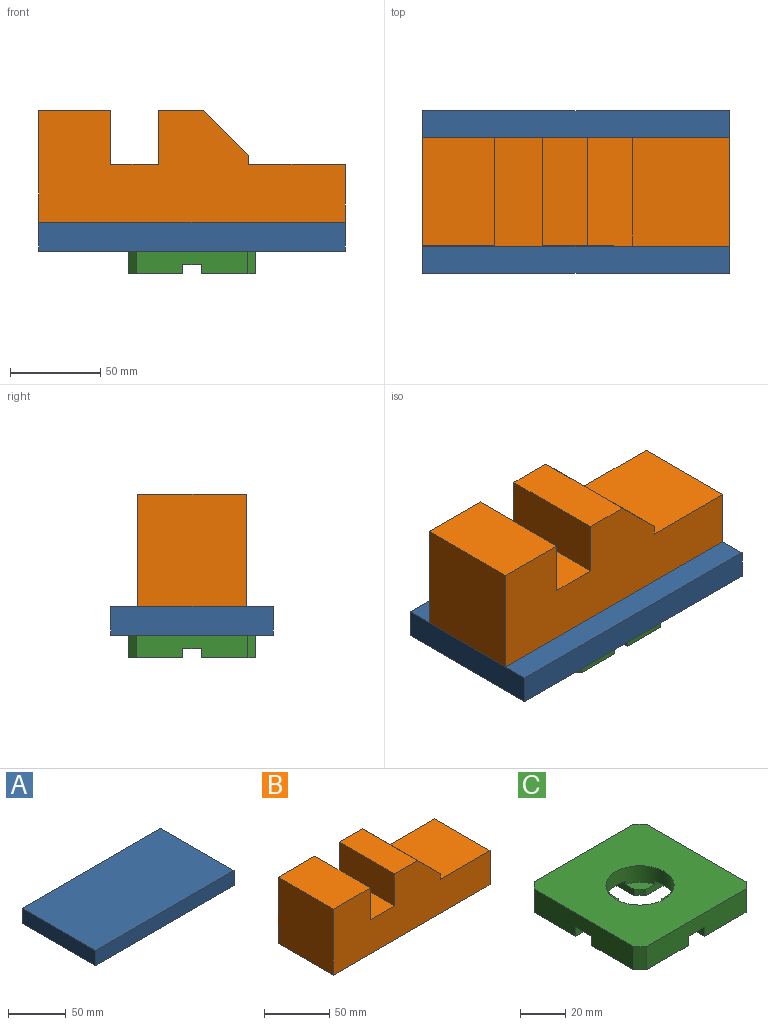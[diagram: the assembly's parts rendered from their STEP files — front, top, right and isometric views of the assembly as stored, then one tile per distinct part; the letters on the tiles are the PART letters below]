
ASSEMBLY  parts=3 mates=2
PART A: 6 faces, bbox 170x90x16 mm
  f0: plane 170x16mm, normal (0,-1,0), area 2720mm2, adj f1,f3,f4,f5
  f1: plane 90x16mm, normal (1,0,0), area 1440mm2, adj f0,f2,f4,f5
  f2: plane 170x16mm, normal (0,1,0), area 2720mm2, adj f1,f3,f4,f5
  f3: plane 90x16mm, normal (-1,0,0), area 1440mm2, adj f0,f2,f4,f5
  f4: plane 170x90mm, normal (0,0,1), area 15300mm2, adj f0,f1,f2,f3
  f5: plane 170x90mm, normal (0,0,-1), area 15300mm2, adj f0,f1,f2,f3
PART B: 13 faces, bbox 170x60x62 mm
  f0: plane 60x32mm, normal (1,0,0), area 1920mm2, adj f1,f10,f11,f12
  f1: plane 60x53.65mm, normal (0,0,1), area 3219.2mm2, adj f0,f2,f11,f12
  f2: plane 60x5.12mm, normal (1,0,0), area 307.4mm2, adj f1,f3,f11,f12
  f3: plane 60x25mm, normal (0.71,0,0.71), area 2116.1mm2, adj f2,f4,f11,f12
  f4: plane 60x25mm, normal (0,0,1), area 1500mm2, adj f3,f5,f11,f12
  f5: plane 60x30mm, normal (-1,0,0), area 1800mm2, adj f4,f6,f11,f12
  f6: plane 60x26.35mm, normal (0,0,1), area 1580.8mm2, adj f5,f7,f11,f12
  f7: plane 60x30mm, normal (1,0,0), area 1800mm2, adj f6,f8,f11,f12
  f8: plane 60x40mm, normal (0,0,1), area 2400mm2, adj f7,f9,f11,f12
  f9: plane 62x60mm, normal (-1,0,0), area 3720mm2, adj f8,f10,f11,f12
  f10: plane 170x60mm, normal (0,0,-1), area 10200mm2, adj f0,f9,f11,f12
  f11: plane 170x62mm, normal (0,-1,0), area 7829mm2, adj f0,f1,f2,f3,f4,f5,f6,f7
  f12: plane 170x62mm, normal (0,1,0), area 7829mm2, adj f0,f1,f2,f3,f4,f5,f6,f7
PART C: 34 faces, bbox 70x70x12.5 mm
  f0: cylinder r=10mm len=3.66mm, axis (0,0,1), area 18.3mm2, adj f7,f16,f19,f26
  f1: cylinder r=10mm len=3.66mm, axis (0,0,1), area 18.3mm2, adj f8,f17,f21,f27
  f2: cylinder r=10mm len=3.66mm, axis (0,0,1), area 18.3mm2, adj f9,f22,f23,f28
  f3: cylinder r=10mm len=3.66mm, axis (0,0,1), area 18.3mm2, adj f15,f18,f24,f29
  f4: plane 20.86x10mm, normal (0,0,-1), area 202.8mm2, adj f11,f23,f24,f25
  f5: plane 20.86x10mm, normal (0,0,-1), area 202.8mm2, adj f10,f18,f19,f25
  f6: plane 20.86x10mm, normal (0,0,-1), area 202.8mm2, adj f13,f16,f17,f25
  f7: plane 30x30mm, normal (0,0,-1), area 884.1mm2, adj f0,f10,f13,f16,f19,f30
  f8: plane 30x30mm, normal (0,0,-1), area 884.1mm2, adj f1,f12,f13,f17,f21,f33
  f9: plane 30x30mm, normal (0,0,-1), area 884.1mm2, adj f2,f11,f12,f22,f23,f32
  f10: plane 62x12.5mm, normal (1,0,0), area 725mm2, adj f5,f7,f14,f15,f18,f19,f30,f31
  f11: plane 62x12.5mm, normal (0,1,0), area 725mm2, adj f4,f9,f14,f15,f23,f24,f31,f32
  f12: plane 62x12.5mm, normal (-1,0,0), area 725mm2, adj f8,f9,f14,f20,f21,f22,f32,f33
  f13: plane 62x12.5mm, normal (0,-1,0), area 725mm2, adj f6,f7,f8,f14,f16,f17,f30,f33
  f14: plane 70x70mm, normal (0,0,1), area 4161.1mm2, adj f10,f11,f12,f13,f25,f30,f31,f32
  f15: plane 30x30mm, normal (0,0,-1), area 884.1mm2, adj f3,f10,f11,f18,f24,f31
  f16: plane 26.34x5mm, normal (-1,0,0), area 123.5mm2, adj f0,f6,f7,f13,f25,f26
  f17: plane 26.34x5mm, normal (1,0,0), area 123.5mm2, adj f1,f6,f8,f13,f25,f27
  f18: plane 26.34x5mm, normal (0,-1,0), area 123.5mm2, adj f3,f5,f10,f15,f25,f29
  f19: plane 26.34x5mm, normal (0,1,0), area 123.5mm2, adj f0,f5,f7,f10,f25,f26
  f20: plane 20.86x10mm, normal (0,0,-1), area 202.8mm2, adj f12,f21,f22,f25
  f21: plane 26.34x5mm, normal (0,1,0), area 123.5mm2, adj f1,f8,f12,f20,f25,f27
  f22: plane 26.34x5mm, normal (0,-1,0), area 123.5mm2, adj f2,f9,f12,f20,f25,f28
  f23: plane 26.34x5mm, normal (1,0,0), area 123.5mm2, adj f2,f4,f9,f11,f25,f28
  f24: plane 26.34x5mm, normal (-1,0,0), area 123.5mm2, adj f3,f4,f11,f15,f25,f29
  f25: cylinder r=15mm len=30mm, axis (0,0,1), area 787.1mm2, adj f4,f5,f6,f14,f16,f17,f18,f19
  f26: plane 9.14x9.14mm, normal (0,0,1), area 46.7mm2, adj f0,f16,f19,f25
  f27: plane 9.14x9.14mm, normal (0,0,1), area 46.7mm2, adj f1,f17,f21,f25
  f28: plane 9.14x9.14mm, normal (0,0,1), area 46.7mm2, adj f2,f22,f23,f25
  f29: plane 9.14x9.14mm, normal (0,0,1), area 46.7mm2, adj f3,f18,f24,f25
  f30: plane 12.5x4mm, normal (0.71,-0.71,0), area 70.7mm2, adj f7,f10,f13,f14
  f31: plane 12.5x4mm, normal (0.71,0.71,0), area 70.7mm2, adj f10,f11,f14,f15
  f32: plane 12.5x4mm, normal (-0.71,0.71,0), area 70.7mm2, adj f9,f11,f12,f14
  f33: plane 12.5x4mm, normal (-0.71,-0.71,0), area 70.7mm2, adj f8,f12,f13,f14
PLACE A t=(0,0,12.5)mm
PLACE B t=(0,5,28.5)mm
PLACE C at identity fixed
MATE fastened A.f5 <-> C.f25  axis (0,0,-1) through (0,0,12.5)mm
MATE fastened B.f10 <-> A.f4  axis (0,0,-1) through (0,0,28.5)mm
